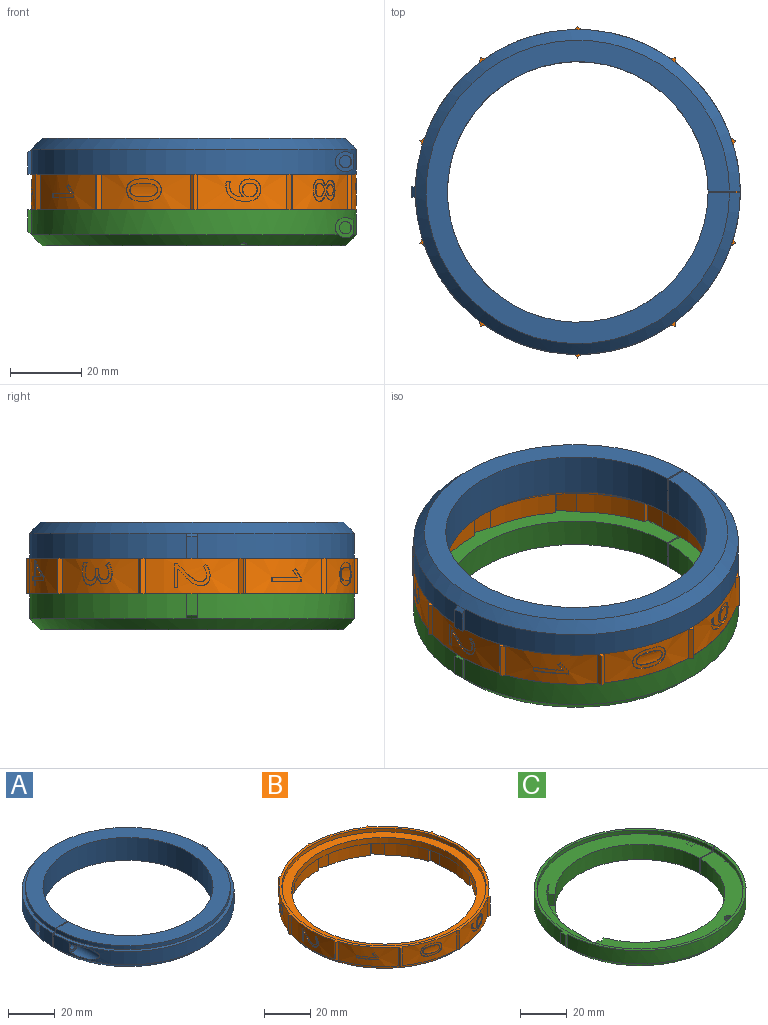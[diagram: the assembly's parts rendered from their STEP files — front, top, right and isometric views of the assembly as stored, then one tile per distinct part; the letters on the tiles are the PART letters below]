
ASSEMBLY  parts=3 mates=2
PART A: 26 faces, bbox 92x91x12 mm
  f0: plane 1.5x0.02mm, normal (0,0,-1), area 0mm2, adj f9,f23,f25
  f1: cylinder r=45.5mm len=90.97mm, axis (0,0,-1), area 970.8mm2, adj f5,f9,f11,f15,f16,f17,f18,f23
  f2: cylinder r=45.5mm len=90.97mm, axis (0,0,-1), area 920.2mm2, adj f5,f9,f10,f13,f14,f21
  f3: cylinder r=1.7mm len=8.75mm, axis (0,1,0), area 93.5mm2, adj f10,f14
  f4: cylinder r=36.5mm len=73mm, axis (0,0,-1), area 2746mm2, adj f6,f8,f10,f11
  f5: plane 92x91mm, normal (0,0,1), area 424mm2, adj f1,f2,f7,f10,f11,f21,f22,f23
  f6: plane 85x85mm, normal (0,0,-1), area 1486.1mm2, adj f4,f9,f10,f11
  f7: cylinder r=44mm len=88mm, axis (0,0,-1), area 551.9mm2, adj f5,f8,f10,f11
  f8: plane 88x88mm, normal (0,0,1), area 1893mm2, adj f4,f7,f10,f11
  f9: cone r=45.5mm half-angle=45deg, axis (0,0,1), area 1170.8mm2, adj f0,f1,f2,f6,f10,f11,f24
  f10: plane 12x9mm, normal (0,1,0), area 91.4mm2, adj f2,f3,f4,f5,f6,f7,f8,f9
  f11: plane 12x9mm, normal (0,-1,0), area 91.4mm2, adj f1,f4,f5,f6,f7,f8,f9,f12
  f12: cylinder r=1.7mm len=8.75mm, axis (0,1,0), area 93.5mm2, adj f11,f18
  f13: cylinder r=2.85mm len=13.32mm, axis (0,1,0), area 118.8mm2, adj f2,f14
  f14: plane 5.7x4.95mm, normal (0,-1,0), area 14.5mm2, adj f2,f3,f13
  f15: plane 3.75x3mm, normal (0,0,1), area 10.2mm2, adj f1,f17,f18,f19
  f16: plane 3.75x3mm, normal (0,0,-1), area 10.2mm2, adj f1,f17,f18,f20
  f17: plane 5.7x4.68mm, normal (0,-1,0), area 22mm2, adj f1,f15,f16,f19,f20
  f18: plane 5.7x5.39mm, normal (0,1,0), area 17mm2, adj f1,f12,f15,f16,f19,f20
  f19: plane 3x2.85mm, normal (-0.87,0,0.5), area 9.9mm2, adj f15,f17,f18,f20
  f20: plane 3x2.85mm, normal (-0.87,0,-0.5), area 9.9mm2, adj f16,f17,f18,f19
  f21: plane 7x1.02mm, normal (0,-1,0), area 6.7mm2, adj f2,f5,f22,f24,f25
  f22: plane 6x3mm, normal (1,0,0), area 18mm2, adj f5,f21,f23,f25
  f23: plane 7x1.02mm, normal (0,1,0), area 6.7mm2, adj f0,f1,f5,f22,f25
  f24: plane 1.5x0.02mm, normal (0,0,-1), area 0mm2, adj f9,f21,f25
  f25: plane 3x1mm, normal (0.71,0,-0.71), area 4.2mm2, adj f0,f21,f22,f23,f24
PART B: 281 faces, bbox 91x93x12 mm
  f0: cylinder r=1mm len=2mm, axis (0,0,-1), area 12.6mm2, adj f1,f39
  f1: plane 2x2mm, normal (0,0,-1), area 3.1mm2, adj f0
  f2: cylinder r=1mm len=2mm, axis (0,0,-1), area 12.6mm2, adj f3,f39
  f3: plane 2x2mm, normal (0,0,-1), area 3.1mm2, adj f2
  f4: cylinder r=1mm len=2mm, axis (0,0,-1), area 12.6mm2, adj f5,f39
  f5: plane 2x2mm, normal (0,0,-1), area 3.1mm2, adj f4
  f6: cylinder r=1mm len=2mm, axis (0,0,-1), area 12.6mm2, adj f7,f39
  f7: plane 2x2mm, normal (0,0,-1), area 3.1mm2, adj f6
  f8: cylinder r=1mm len=2mm, axis (0,0,-1), area 12.6mm2, adj f9,f39
  f9: plane 2x2mm, normal (0,0,-1), area 3.1mm2, adj f8
  f10: cylinder r=1mm len=2mm, axis (0,0,-1), area 12.6mm2, adj f11,f39
  f11: plane 2x2mm, normal (0,0,-1), area 3.1mm2, adj f10
  f12: cylinder r=1mm len=2mm, axis (0,0,-1), area 12.6mm2, adj f13,f39
  f13: plane 2x2mm, normal (0,0,-1), area 3.1mm2, adj f12
  f14: cylinder r=1mm len=2mm, axis (0,0,-1), area 12.6mm2, adj f15,f39
  f15: plane 2x2mm, normal (0,0,-1), area 3.1mm2, adj f14
  f16: cylinder r=1mm len=2mm, axis (0,0,-1), area 12.6mm2, adj f17,f39
  f17: plane 2x2mm, normal (0,0,-1), area 3.1mm2, adj f16
  f18: plane 7x1.23mm, normal (-0.95,0.31,0), area 9.1mm2, adj f19,f39,f268,f278
  f19: plane 7x5.34mm, normal (0.31,0.95,0), area 39.3mm2, adj f18,f39,f268,f270
  f20: plane 7x1.23mm, normal (-0.95,-0.31,0), area 9.1mm2, adj f21,f39,f268,f277
  f21: plane 7x5.34mm, normal (-0.31,0.95,0), area 39.3mm2, adj f20,f39,f268,f278
  f22: plane 7x1.05mm, normal (-0.59,-0.81,0), area 9.1mm2, adj f23,f39,f268,f276
  f23: plane 7x4.54mm, normal (-0.81,0.59,0), area 39.3mm2, adj f22,f39,f268,f277
  f24: plane 7x1.3mm, normal (0,-1,0), area 9.1mm2, adj f25,f39,f268,f275
  f25: plane 7x5.62mm, normal (-1,0,0), area 39.3mm2, adj f24,f39,f268,f276
  f26: plane 7x1.05mm, normal (0.59,-0.81,0), area 9.1mm2, adj f27,f39,f268,f274
  f27: plane 7x4.54mm, normal (-0.81,-0.59,0), area 39.3mm2, adj f26,f39,f268,f275
  f28: plane 7x1.23mm, normal (0.95,-0.31,0), area 9.1mm2, adj f29,f39,f268,f273
  f29: plane 7x5.34mm, normal (-0.31,-0.95,0), area 39.3mm2, adj f28,f39,f268,f274
  f30: plane 7x1.23mm, normal (0.95,0.31,0), area 9.1mm2, adj f31,f39,f268,f272
  f31: plane 7x5.34mm, normal (0.31,-0.95,0), area 39.3mm2, adj f30,f39,f268,f273
  f32: plane 7x1.05mm, normal (0.59,0.81,0), area 9.1mm2, adj f33,f39,f268,f271
  f33: plane 7x4.54mm, normal (0.81,-0.59,0), area 39.3mm2, adj f32,f39,f268,f272
  f34: plane 7x1.3mm, normal (0,1,0), area 9.1mm2, adj f35,f39,f268,f269
  f35: plane 7x5.62mm, normal (1,0,0), area 39.3mm2, adj f34,f39,f268,f271
  f36: plane 7x1.05mm, normal (-0.59,0.81,0), area 9.1mm2, adj f37,f39,f268,f270
  f37: plane 7x4.54mm, normal (0.81,0.59,0), area 39.3mm2, adj f36,f39,f268,f269
  f38: cylinder r=40mm len=80mm, axis (0,0,-1), area 754mm2, adj f54,f268
  f39: plane 88x88mm, normal (0,0,-1), area 737.2mm2, adj f0,f2,f4,f6,f8,f10,f12,f14
  f40: cylinder r=45.5mm len=26.21mm, axis (0,0,-1), area 247.6mm2, adj f50,f51,f240,f241,f242,f243,f244,f245
  f41: cylinder r=45.5mm len=21.21mm, axis (0,0,-1), area 225.9mm2, adj f50,f51,f221,f222,f223,f224,f225,f226
  f42: cylinder r=45.5mm len=24.93mm, axis (0,0,-1), area 243.7mm2, adj f50,f51,f198,f199,f200,f201,f202,f203
  f43: cylinder r=45.5mm len=24.93mm, axis (0,0,-1), area 231.8mm2, adj f50,f51,f182,f183,f184,f185,f186,f187
  f44: cylinder r=45.5mm len=21.21mm, axis (0,0,-1), area 242.3mm2, adj f50,f51,f155,f156,f157,f158,f159,f160
  f45: cylinder r=45.5mm len=26.21mm, axis (0,0,-1), area 244.2mm2, adj f50,f51,f134,f135,f136,f137,f138,f139
  f46: cylinder r=45.5mm len=21.21mm, axis (0,0,-1), area 251.4mm2, adj f50,f51,f124,f125,f126,f127,f128,f129
  f47: cylinder r=45.5mm len=24.93mm, axis (0,0,-1), area 214.8mm2, adj f50,f51,f113,f114,f115,f116,f120,f121
  f48: cylinder r=45.5mm len=21.21mm, axis (0,0,-1), area 223.1mm2, adj f50,f51,f87,f88,f89,f90,f91,f92
  f49: cylinder r=45.5mm len=24.93mm, axis (0,0,-1), area 225.9mm2, adj f50,f51,f60,f61,f62,f63,f64,f65
  f50: plane 92.98x91mm, normal (0,0,1), area 362.3mm2, adj f40,f41,f42,f43,f44,f45,f46,f47
  f51: plane 92.98x91mm, normal (0,0,-1), area 431.6mm2, adj f40,f41,f42,f43,f44,f45,f46,f47
  f52: cylinder r=44mm len=88mm, axis (0,0,1), area 552.9mm2, adj f39,f51
  f53: cylinder r=44.25mm len=88.5mm, axis (0,0,1), area 556.1mm2, adj f50,f54
  f54: plane 88.5x88.5mm, normal (0,0,1), area 1124.9mm2, adj f38,f53
  f55: extruded ~1.74x0.9mm, area 0.5mm2, adj f56,f73,f77,f78
  f56: extruded ~1.35x0.67mm, area 0.5mm2, adj f55,f57,f77,f78
  f57: extruded ~1.45x0.83mm, area 0.5mm2, adj f56,f58,f77,f78
  f58: extruded ~1.81x0.92mm, area 0.6mm2, adj f57,f59,f77,f78
  f59: extruded ~1.29x0.69mm, area 0.4mm2, adj f58,f72,f77,f78
  f60: extruded ~1.17x0.34mm, area 0.4mm2, adj f49,f61,f75,f77
  f61: extruded ~5.72x4.33mm, area 2.5mm2, adj f49,f60,f62,f77
  f62: extruded ~3.2x1.43mm, area 1mm2, adj f49,f61,f63,f77
  f63: extruded ~2.36x1.23mm, area 0.8mm2, adj f49,f62,f64,f77
  f64: extruded ~2.2x0.97mm, area 0.7mm2, adj f49,f63,f65,f77
  f65: extruded ~2.46x1.19mm, area 0.8mm2, adj f49,f64,f66,f77
  f66: extruded ~2.21x1mm, area 0.7mm2, adj f49,f65,f67,f77
  f67: extruded ~2.07x0.86mm, area 0.7mm2, adj f49,f66,f68,f77
  f68: extruded ~2.09x1.2mm, area 0.8mm2, adj f49,f67,f69,f77
  f69: plane 0.29x0.09mm, normal (0.95,0.31,0), area 0mm2, adj f49,f68,f70,f77
  f70: extruded ~3.01x1.33mm, area 1mm2, adj f49,f69,f71,f77
  f71: extruded ~2.28x1.03mm, area 0.8mm2, adj f49,f70,f76,f77
  f72: extruded ~1.45x0.62mm, area 0.5mm2, adj f59,f74,f77,f78
  f73: extruded ~1.54x0.78mm, area 0.5mm2, adj f55,f74,f77,f78
  f74: extruded ~1.33x0.6mm, area 0.4mm2, adj f72,f73,f77,f78
  f75: plane 1.13x0.51mm, normal (0,0,-1), area 0.3mm2, adj f49,f60,f76,f77
  f76: extruded ~1.13x0.35mm, area 0.3mm2, adj f49,f71,f75,f77
  f77: cylinder r=45.5mm len=9.7mm, axis (0,0,-1), area 26.6mm2, adj f55,f56,f57,f58,f59,f60,f61,f62
  f78: cylinder r=45.5mm len=4.07mm, axis (0,0,-1), area 12mm2, adj f55,f56,f57,f58,f59,f72,f73,f74
  f79: plane 0.26x0.22mm, normal (0.53,0.73,-0.43), area 0.1mm2, adj f80,f99,f105,f106
  f80: extruded ~1.45x0.94mm, area 0.4mm2, adj f79,f81,f105,f106
  f81: extruded ~1.05x0.88mm, area 0.3mm2, adj f80,f82,f105,f106
  f82: extruded ~1.2x1mm, area 0.3mm2, adj f81,f98,f105,f106
  f83: extruded ~1.26x0.85mm, area 0.4mm2, adj f84,f103,f105,f107
  f84: extruded ~1.01x0.85mm, area 0.3mm2, adj f83,f85,f105,f107
  f85: extruded ~1.03x0.87mm, area 0.3mm2, adj f84,f86,f105,f107
  f86: extruded ~1.14x0.46mm, area 0.3mm2, adj f85,f96,f105,f107
  f87: extruded ~2.16x1.78mm, area 0.8mm2, adj f48,f88,f101,f105
  f88: extruded ~1.64x1.34mm, area 0.5mm2, adj f48,f87,f89,f105
  f89: extruded ~2.02x0.71mm, area 0.5mm2, adj f48,f88,f90,f105
  f90: extruded ~2x0.71mm, area 0.5mm2, adj f48,f89,f91,f105
  f91: extruded ~1.63x1.33mm, area 0.5mm2, adj f48,f90,f92,f105
  f92: extruded ~2.22x1.74mm, area 0.8mm2, adj f48,f91,f93,f105
  f93: extruded ~2.34x1.91mm, area 0.9mm2, adj f48,f92,f94,f105
  f94: extruded ~1.82x1.48mm, area 0.6mm2, adj f48,f93,f95,f105
  f95: extruded ~2.29x0.76mm, area 0.6mm2, adj f48,f94,f97,f105
  f96: extruded ~1.17x0.46mm, area 0.3mm2, adj f86,f104,f105,f107
  f97: extruded ~2.26x0.8mm, area 0.6mm2, adj f48,f95,f102,f105
  f98: extruded ~1.43x0.53mm, area 0.4mm2, adj f82,f100,f105,f106
  f99: extruded ~1.97x1.72mm, area 0.7mm2, adj f79,f100,f105,f106
  f100: extruded ~1.87x1.53mm, area 0.7mm2, adj f98,f99,f105,f106
  f101: extruded ~2.34x2.09mm, area 0.9mm2, adj f48,f87,f102,f105
  f102: extruded ~1.83x1.48mm, area 0.6mm2, adj f48,f97,f101,f105
  f103: extruded ~1.71x1.57mm, area 0.7mm2, adj f83,f104,f105,f107
  f104: extruded ~1.03x0.87mm, area 0.3mm2, adj f96,f103,f105,f107
  f105: cylinder r=45.5mm len=8.25mm, axis (0,0,-1), area 30.7mm2, adj f79,f80,f81,f82,f83,f84,f85,f86
  f106: cylinder r=45.5mm len=3.8mm, axis (0,0,-1), area 10.9mm2, adj f79,f80,f81,f82,f98,f99,f100
  f107: cylinder r=45.5mm len=3.17mm, axis (0,0,-1), area 6.8mm2, adj f83,f84,f85,f86,f96,f103,f104
  f108: extruded ~1.44x1mm, area 0.5mm2, adj f109,f118,f122,f123
  f109: extruded ~3.07x1.3mm, area 0.8mm2, adj f108,f110,f122,f123
  f110: extruded ~3.05x1.29mm, area 0.8mm2, adj f109,f111,f122,f123
  f111: extruded ~1.44x1mm, area 0.5mm2, adj f110,f112,f122,f123
  f112: extruded ~1.46x1.01mm, area 0.5mm2, adj f111,f117,f122,f123
  f113: extruded ~5.03x3.18mm, area 1.7mm2, adj f47,f114,f120,f122
  f114: extruded ~3.73x1.56mm, area 1mm2, adj f47,f113,f115,f122
  f115: extruded ~2.38x1.37mm, area 0.7mm2, adj f47,f114,f116,f122
  f116: extruded ~5.02x3.16mm, area 1.7mm2, adj f47,f115,f121,f122
  f117: extruded ~3.05x1.29mm, area 0.8mm2, adj f112,f119,f122,f123
  f118: extruded ~1.46x1.01mm, area 0.5mm2, adj f108,f119,f122,f123
  f119: extruded ~3.06x1.3mm, area 0.8mm2, adj f117,f118,f122,f123
  f120: extruded ~2.35x1.37mm, area 0.7mm2, adj f47,f113,f121,f122
  f121: extruded ~3.74x1.56mm, area 1mm2, adj f47,f116,f120,f122
  f122: cylinder r=45.5mm len=9.71mm, axis (0,0,-1), area 27.5mm2, adj f108,f109,f110,f111,f112,f113,f114,f115
  f123: cylinder r=45.5mm len=7.7mm, axis (0,0,-1), area 23.7mm2, adj f108,f109,f110,f111,f112,f117,f118,f119
  f124: plane 1.19x0.2mm, normal (0.59,-0.81,0), area 0.3mm2, adj f46,f125,f131,f133
  f125: plane 8.17x6.02mm, normal (0,0,1), area 2.5mm2, adj f46,f124,f126,f133
  f126: plane 1.02x0.2mm, normal (-0.59,0.81,0), area 0.3mm2, adj f46,f125,f132,f133
  f127: plane 0.79x0.73mm, normal (0.36,-0.5,-0.79), area 0.3mm2, adj f46,f128,f132,f133
  f128: plane 1x0.78mm, normal (0.45,-0.63,0.63), area 0.3mm2, adj f46,f127,f129,f133
  f129: extruded ~0.82x0.8mm, area 0.3mm2, adj f46,f128,f130,f133
  f130: extruded ~2.2x1.75mm, area 0.6mm2, adj f46,f129,f131,f133
  f131: plane 5.31x3.63mm, normal (0,0,-1), area 1.5mm2, adj f46,f124,f130,f133
  f132: plane 2.6x1.69mm, normal (-0.46,0.64,-0.62), area 0.8mm2, adj f46,f126,f127,f133
  f133: cylinder r=45.5mm len=8.03mm, axis (0,0,-1), area 14.5mm2, adj f124,f125,f126,f127,f128,f129,f130,f131
  f134: plane 1.04x0.35mm, normal (0,0,1), area 0.3mm2, adj f45,f135,f152,f154
  f135: plane 5.1x0.25mm, normal (0,1,0), area 1.3mm2, adj f45,f134,f136,f154
  f136: plane 0.25x0.05mm, normal (0,0,1), area 0mm2, adj f45,f135,f137,f154
  f137: plane 2.17x2.12mm, normal (0,-0.71,0.7), area 0.8mm2, adj f45,f136,f138,f154
  f138: extruded ~2.33x1.98mm, area 0.8mm2, adj f45,f137,f139,f154
  f139: extruded ~1.87x0.53mm, area 0.5mm2, adj f45,f138,f140,f154
  f140: extruded ~1.92x0.79mm, area 0.5mm2, adj f45,f139,f141,f154
  f141: extruded ~2.19x0.72mm, area 0.6mm2, adj f45,f140,f142,f154
  f142: extruded ~2.98x1.14mm, area 0.8mm2, adj f45,f141,f143,f154
  f143: plane 0.77x0.6mm, normal (0,-0.61,-0.79), area 0.2mm2, adj f45,f142,f144,f154
  f144: extruded ~1.23x0.74mm, area 0.4mm2, adj f45,f143,f145,f154
  f145: extruded ~1.17x0.27mm, area 0.3mm2, adj f45,f144,f146,f154
  f146: extruded ~1.34x0.46mm, area 0.4mm2, adj f45,f145,f147,f154
  f147: extruded ~1.26x0.48mm, area 0.3mm2, adj f45,f146,f148,f154
  f148: extruded ~1.05x0.29mm, area 0.3mm2, adj f45,f147,f149,f154
  f149: extruded ~1x0.57mm, area 0.3mm2, adj f45,f148,f150,f154
  f150: extruded ~1.72x1.57mm, area 0.6mm2, adj f45,f149,f151,f154
  f151: plane 2.63x2.61mm, normal (0,0.71,-0.71), area 0.9mm2, adj f45,f150,f153,f154
  f152: plane 6.52x0.25mm, normal (0,-1,0), area 1.6mm2, adj f45,f134,f153,f154
  f153: plane 0.97x0.35mm, normal (0,0,-1), area 0.2mm2, adj f45,f151,f152,f154
  f154: cylinder r=45.5mm len=10.06mm, axis (0,0,-1), area 21.7mm2, adj f134,f135,f136,f137,f138,f139,f140,f141
  f155: extruded ~1.59x0.81mm, area 0.5mm2, adj f44,f156,f176,f178
  f156: extruded ~1.45x1.17mm, area 0.4mm2, adj f44,f155,f157,f178
  f157: extruded ~1.68x1.37mm, area 0.5mm2, adj f44,f156,f158,f178
  f158: extruded ~2.18x0.73mm, area 0.6mm2, adj f44,f157,f159,f178
  f159: extruded ~2.96x1.03mm, area 0.8mm2, adj f44,f158,f160,f178
  f160: plane 0.87x0.65mm, normal (-0.35,-0.48,-0.81), area 0.3mm2, adj f44,f159,f161,f178
  f161: extruded ~2.33x0.85mm, area 0.6mm2, adj f44,f160,f162,f178
  f162: extruded ~1.23x0.49mm, area 0.3mm2, adj f44,f161,f163,f178
  f163: extruded ~1.08x0.91mm, area 0.3mm2, adj f44,f162,f164,f178
  f164: extruded ~1.28x1.05mm, area 0.4mm2, adj f44,f163,f165,f178
  f165: extruded ~1.68x0.57mm, area 0.4mm2, adj f44,f164,f166,f178
  f166: plane 0.9x0.2mm, normal (0.59,0.81,0), area 0.2mm2, adj f44,f165,f167,f178
  f167: plane 0.98x0.8mm, normal (0,0,-1), area 0.3mm2, adj f44,f166,f168,f178
  f168: plane 0.9x0.2mm, normal (-0.59,-0.81,0), area 0.2mm2, adj f44,f167,f169,f178
  f169: extruded ~2.58x1.59mm, area 0.9mm2, adj f44,f168,f170,f178
  f170: extruded ~2.4x1.81mm, area 0.9mm2, adj f44,f169,f171,f178
  f171: extruded ~2.6x0.71mm, area 0.7mm2, adj f44,f170,f172,f178
  f172: plane 1.02x0.96mm, normal (0,0,-1), area 0.3mm2, adj f44,f171,f173,f178
  f173: extruded ~2.63x0.61mm, area 0.7mm2, adj f44,f172,f174,f178
  f174: extruded ~2.71x0.84mm, area 0.7mm2, adj f44,f173,f175,f178
  f175: extruded ~1.99x1.6mm, area 0.6mm2, adj f44,f174,f177,f178
  f176: plane 0.23x0.18mm, normal (0,0,1), area 0mm2, adj f44,f155,f177,f178
  f177: extruded ~2.45x2.09mm, area 0.9mm2, adj f44,f175,f176,f178
  f178: cylinder r=45.5mm len=8.24mm, axis (0,0,-1), area 23.6mm2, adj f155,f156,f157,f158,f159,f160,f161,f162
  f179: plane 3.37x0.24mm, normal (0.95,0.31,0), area 0.8mm2, adj f180,f192,f196,f197
  f180: plane 3.99x2.79mm, normal (-0.53,-0.17,0.83), area 1.2mm2, adj f179,f181,f196,f197
  f181: extruded ~1.26x0.69mm, area 0.3mm2, adj f180,f191,f196,f197
  f182: plane 1.17x0.53mm, normal (0,0,1), area 0.3mm2, adj f43,f183,f194,f196
  f183: plane 1.45x0.24mm, normal (0.95,0.31,0), area 0.4mm2, adj f43,f182,f184,f196
  f184: plane 6.3x2.51mm, normal (0,0,1), area 1.7mm2, adj f43,f183,f185,f196
  f185: plane 1.27x0.24mm, normal (0.95,0.31,0), area 0.3mm2, adj f43,f184,f186,f196
  f186: plane 6.35x4.51mm, normal (0.53,0.17,-0.83), area 2mm2, adj f43,f185,f187,f196
  f187: plane 1.12x0.52mm, normal (0,0,-1), area 0.3mm2, adj f43,f186,f188,f196
  f188: plane 4.58x0.24mm, normal (-0.95,-0.31,0), area 1.1mm2, adj f43,f187,f189,f196
  f189: plane 2.25x0.74mm, normal (0,0,-1), area 0.6mm2, adj f43,f188,f190,f196
  f190: plane 1.19x0.24mm, normal (-0.95,-0.31,0), area 0.3mm2, adj f43,f189,f195,f196
  f191: plane 0.24x0.08mm, normal (-0.95,-0.31,0), area 0mm2, adj f181,f193,f196,f197
  f192: plane 2.38x0.96mm, normal (0,0,-1), area 0.6mm2, adj f179,f193,f196,f197
  f193: extruded ~2.91x1.28mm, area 0.7mm2, adj f191,f192,f196,f197
  f194: plane 1.45x0.24mm, normal (-0.95,-0.31,0), area 0.4mm2, adj f43,f182,f195,f196
  f195: plane 2.25x0.74mm, normal (0,0,1), area 0.6mm2, adj f43,f190,f194,f196
  f196: cylinder r=45.5mm len=9.48mm, axis (0,0,-1), area 25.5mm2, adj f179,f180,f181,f182,f183,f184,f185,f186
  f197: cylinder r=45.5mm len=5.04mm, axis (0,0,-1), area 8.6mm2, adj f179,f180,f181,f191,f192,f193
  f198: extruded ~2.41x0.61mm, area 0.6mm2, adj f42,f199,f213,f215
  f199: extruded ~2.64x0.93mm, area 0.7mm2, adj f42,f198,f200,f215
  f200: extruded ~2.46x1.15mm, area 0.7mm2, adj f42,f199,f201,f215
  f201: extruded ~2.11x0.93mm, area 0.6mm2, adj f42,f200,f202,f215
  f202: extruded ~2.3x0.82mm, area 0.6mm2, adj f42,f201,f203,f215
  f203: extruded ~1.42x0.28mm, area 0.4mm2, adj f42,f202,f204,f215
  f204: plane 2.82x0.97mm, normal (-0.09,0.03,1), area 0.7mm2, adj f42,f203,f205,f215
  f205: plane 3.61x0.24mm, normal (-0.95,0.31,0), area 0.9mm2, adj f42,f204,f206,f215
  f206: plane 1.18x0.48mm, normal (0,0,1), area 0.3mm2, adj f42,f205,f207,f215
  f207: plane 4.68x0.24mm, normal (0.95,-0.31,0), area 1.2mm2, adj f42,f206,f208,f215
  f208: plane 4.6x1.43mm, normal (0.08,-0.02,-1), area 1.2mm2, adj f42,f207,f209,f215
  f209: plane 0.61x0.44mm, normal (-0.8,0.26,-0.53), area 0.2mm2, adj f42,f208,f210,f215
  f210: extruded ~1.57x0.29mm, area 0.4mm2, adj f42,f209,f211,f215
  f211: extruded ~2.33x1.99mm, area 0.9mm2, adj f42,f210,f212,f215
  f212: extruded ~2.28x2.15mm, area 0.9mm2, adj f42,f211,f214,f215
  f213: plane 1.16x0.7mm, normal (0,0,-1), area 0.3mm2, adj f42,f198,f214,f215
  f214: extruded ~2.44x0.71mm, area 0.6mm2, adj f42,f212,f213,f215
  f215: cylinder r=45.5mm len=9.55mm, axis (0,0,-1), area 22.2mm2, adj f198,f199,f200,f201,f202,f203,f204,f205
  f216: extruded ~1.58x1.28mm, area 0.4mm2, adj f217,f234,f238,f239
  f217: extruded ~1.35x0.66mm, area 0.4mm2, adj f216,f218,f238,f239
  f218: extruded ~1.44x0.79mm, area 0.4mm2, adj f217,f219,f238,f239
  f219: extruded ~1.64x1.33mm, area 0.5mm2, adj f218,f220,f238,f239
  f220: extruded ~1.18x0.96mm, area 0.4mm2, adj f219,f233,f238,f239
  f221: extruded ~1.17x0.29mm, area 0.3mm2, adj f41,f222,f236,f238
  f222: extruded ~5.02x4.33mm, area 2.1mm2, adj f41,f221,f223,f238
  f223: extruded ~2.86x2.24mm, area 0.9mm2, adj f41,f222,f224,f238
  f224: extruded ~2.36x1.14mm, area 0.7mm2, adj f41,f223,f225,f238
  f225: extruded ~2.19x0.92mm, area 0.6mm2, adj f41,f224,f226,f238
  f226: extruded ~2.22x1.77mm, area 0.7mm2, adj f41,f225,f227,f238
  f227: extruded ~1.95x1.53mm, area 0.6mm2, adj f41,f226,f228,f238
  f228: extruded ~2.07x0.81mm, area 0.6mm2, adj f41,f227,f229,f238
  f229: extruded ~2.08x1.09mm, area 0.6mm2, adj f41,f228,f230,f238
  f230: plane 0.2x0.15mm, normal (0.59,-0.81,0), area 0mm2, adj f41,f229,f231,f238
  f231: extruded ~2.66x2.07mm, area 0.8mm2, adj f41,f230,f232,f238
  f232: extruded ~2.28x0.97mm, area 0.6mm2, adj f41,f231,f237,f238
  f233: extruded ~1.44x0.59mm, area 0.4mm2, adj f220,f235,f238,f239
  f234: extruded ~1.39x1.12mm, area 0.4mm2, adj f216,f235,f238,f239
  f235: extruded ~1.33x0.58mm, area 0.4mm2, adj f233,f234,f238,f239
  f236: plane 0.94x0.9mm, normal (0,0,1), area 0.3mm2, adj f41,f221,f237,f238
  f237: extruded ~1.13x0.31mm, area 0.3mm2, adj f41,f232,f236,f238
  f238: cylinder r=45.5mm len=8.25mm, axis (0,0,-1), area 26.7mm2, adj f216,f217,f218,f219,f220,f221,f222,f223
  f239: cylinder r=45.5mm len=3.82mm, axis (0,0,-1), area 12mm2, adj f216,f217,f218,f219,f220,f233,f234,f235
  f240: plane 1.32x0.25mm, normal (0,1,0), area 0.3mm2, adj f40,f241,f245,f247
  f241: plane 8.94x3.77mm, normal (0,0.39,0.92), area 2.4mm2, adj f40,f240,f246,f247
  f242: plane 6.37x0.25mm, normal (0,-1,0), area 1.6mm2, adj f40,f243,f246,f247
  f243: plane 1.13x0.36mm, normal (0,0,-1), area 0.3mm2, adj f40,f242,f244,f247
  f244: plane 5.11x0.25mm, normal (0,1,0), area 1.3mm2, adj f40,f243,f245,f247
  f245: plane 8.79x3.82mm, normal (0,-0.4,-0.92), area 2.4mm2, adj f40,f240,f244,f247
  f246: plane 0.98x0.35mm, normal (0,0,1), area 0.2mm2, adj f40,f241,f242,f247
  f247: cylinder r=45.5mm len=9.92mm, axis (0,0,-1), area 18.3mm2, adj f240,f241,f242,f243,f244,f245,f246
  f248: plane 10x1mm, normal (-0.71,0.71,0), area 14.1mm2, adj f43,f50,f51,f249
  f249: plane 10x1mm, normal (0.71,0.71,0), area 14.1mm2, adj f42,f50,f51,f248
  f250: plane 10x1.4mm, normal (-0.99,0.16,0), area 14.1mm2, adj f44,f50,f51,f251
  f251: plane 10x1.4mm, normal (0.16,0.99,0), area 14.1mm2, adj f43,f50,f51,f250
  f252: plane 10x1.26mm, normal (-0.89,-0.45,0), area 14.1mm2, adj f45,f50,f51,f253
  f253: plane 10x1.26mm, normal (-0.45,0.89,0), area 14.1mm2, adj f44,f50,f51,f252
  f254: plane 10x1.26mm, normal (-0.45,-0.89,0), area 14.1mm2, adj f46,f50,f51,f255
  f255: plane 10x1.26mm, normal (-0.89,0.45,0), area 14.1mm2, adj f45,f50,f51,f254
  f256: plane 10x1.4mm, normal (0.16,-0.99,0), area 14.1mm2, adj f47,f50,f51,f257
  f257: plane 10x1.4mm, normal (-0.99,-0.16,0), area 14.1mm2, adj f46,f50,f51,f256
  f258: plane 10x1mm, normal (0.71,-0.71,0), area 14.1mm2, adj f49,f50,f51,f259
  f259: plane 10x1mm, normal (-0.71,-0.71,0), area 14.1mm2, adj f47,f50,f51,f258
  f260: plane 10x1.4mm, normal (0.99,-0.16,0), area 14.1mm2, adj f48,f50,f51,f261
  f261: plane 10x1.4mm, normal (-0.16,-0.99,0), area 14.1mm2, adj f49,f50,f51,f260
  f262: plane 10x1.26mm, normal (0.89,0.45,0), area 14.1mm2, adj f40,f50,f51,f263
  f263: plane 10x1.26mm, normal (0.45,-0.89,0), area 14.1mm2, adj f48,f50,f51,f262
  f264: plane 10x1.26mm, normal (0.45,0.89,0), area 14.1mm2, adj f41,f50,f51,f265
  f265: plane 10x1.26mm, normal (0.89,-0.45,0), area 14.1mm2, adj f40,f50,f51,f264
  f266: plane 10x1.4mm, normal (-0.16,0.99,0), area 14.1mm2, adj f42,f50,f51,f267
  f267: plane 10x1.4mm, normal (0.99,0.16,0), area 14.1mm2, adj f41,f50,f51,f266
  f268: plane 84.45x82mm, normal (0,0,-1), area 286.9mm2, adj f18,f19,f20,f21,f22,f23,f24,f25
  f269: cylinder r=41mm len=16.97mm, axis (0,0,-1), area 139.9mm2, adj f34,f37,f39,f268
  f270: cylinder r=41mm len=18.22mm, axis (0,0,-1), area 139.9mm2, adj f19,f36,f39,f268
  f271: cylinder r=41mm len=19.72mm, axis (0,0,-1), area 139.9mm2, adj f32,f35,f39,f268
  f272: cylinder r=41mm len=14.94mm, axis (0,0,-1), area 139.9mm2, adj f30,f33,f39,f268
  f273: cylinder r=41mm len=19.29mm, axis (0,0,-1), area 139.9mm2, adj f28,f31,f39,f268
  f274: cylinder r=41mm len=18.22mm, axis (0,0,-1), area 139.9mm2, adj f26,f29,f39,f268
  f275: cylinder r=41mm len=16.97mm, axis (0,0,-1), area 139.9mm2, adj f24,f27,f39,f268
  f276: cylinder r=41mm len=19.72mm, axis (0,0,-1), area 139.9mm2, adj f22,f25,f39,f268
  f277: cylinder r=41mm len=14.94mm, axis (0,0,-1), area 139.9mm2, adj f20,f23,f39,f268
  f278: cylinder r=41mm len=19.29mm, axis (0,0,-1), area 139.9mm2, adj f18,f21,f39,f268
  f279: cylinder r=1mm len=2mm, axis (0,0,-1), area 12.6mm2, adj f39,f280
  f280: plane 2x2mm, normal (0,0,-1), area 3.1mm2, adj f279
PART C: 42 faces, bbox 92x91x10 mm
  f0: cylinder r=45.5mm len=90.97mm, axis (0,0,-1), area 974.7mm2, adj f1,f8,f26,f27,f32,f35,f40
  f1: cone r=45.5mm half-angle=45deg, axis (0,0,1), area 1155.1mm2, adj f0,f2,f3,f9,f22,f26,f27,f31
  f2: plane 1.5x0.02mm, normal (0,0,-1), area 0mm2, adj f1,f37,f39
  f3: cylinder r=45.5mm len=90.97mm, axis (0,0,-1), area 926.5mm2, adj f1,f8,f22,f23,f33,f37
  f4: plane 45.99x17.02mm, normal (0,0,1), area 159.5mm2, adj f5,f7,f12,f13,f14,f19,f20,f21
  f5: cylinder r=39.5mm len=6mm, axis (0,0,1), area 9.2mm2, adj f4,f6,f13,f34
  f6: plane 88.5x88.5mm, normal (0,0,1), area 1791.4mm2, adj f5,f7,f10,f12,f13,f14,f15,f19
  f7: cylinder r=36.5mm len=73mm, axis (0,0,-1), area 1586.4mm2, adj f4,f6,f9,f21,f32,f33,f34
  f8: plane 92x91mm, normal (0,0,1), area 354.8mm2, adj f0,f3,f10,f32,f33,f35,f36,f37
  f9: plane 85x85mm, normal (0,0,-1), area 1484.1mm2, adj f1,f7,f32,f33,f41
  f10: cylinder r=44.25mm len=88.5mm, axis (0,0,1), area 555.1mm2, adj f6,f8,f32,f33
  f11: cylinder r=1.7mm len=8.75mm, axis (0,-1,0), area 93.5mm2, adj f23,f33
  f12: plane 12x6mm, normal (1,0,0), area 72mm2, adj f4,f6,f13,f14
  f13: plane 6x2.37mm, normal (0,1,0), area 14.2mm2, adj f4,f5,f6,f12
  f14: cylinder r=40mm len=32.54mm, axis (0,0,1), area 228mm2, adj f4,f6,f12,f19
  f15: cylinder r=1.9mm len=3.8mm, axis (0,0,1), area 11.9mm2, adj f6,f16
  f16: plane 3.8x3.8mm, normal (0,0,1), area 3.8mm2, adj f15,f18
  f17: plane 3.1x3.1mm, normal (0,0,1), area 4.4mm2, adj f18,f41
  f18: cylinder r=1.55mm len=3.2mm, axis (0,0,1), area 31.2mm2, adj f16,f17
  f19: plane 6x0.41mm, normal (-0.81,-0.58,0), area 3mm2, adj f4,f6,f14,f20
  f20: cylinder r=39.5mm len=6mm, axis (0,0,1), area 43.1mm2, adj f4,f6,f19,f21
  f21: plane 6x2.16mm, normal (-0.69,-0.72,0), area 18mm2, adj f4,f6,f7,f20
  f22: cylinder r=2.85mm len=13.32mm, axis (0,1,0), area 110.8mm2, adj f1,f3,f23
  f23: plane 5.7x4.95mm, normal (0,-1,0), area 14.5mm2, adj f3,f11,f22
  f24: cylinder r=1.7mm len=8.75mm, axis (0,-1,0), area 93.5mm2, adj f27,f32
  f25: plane 3x0.42mm, normal (-0.87,0,-0.5), area 1.5mm2, adj f26,f27,f28,f40
  f26: plane 5.7x5.18mm, normal (0,-1,0), area 24.4mm2, adj f0,f1,f25,f28,f29,f30,f31
  f27: plane 5.89x5.7mm, normal (0,1,0), area 19.1mm2, adj f0,f1,f24,f25,f28,f29,f30,f31
  f28: plane 3.29x3mm, normal (0,0,-1), area 9.9mm2, adj f25,f26,f27,f29
  f29: plane 3x2.85mm, normal (0.87,0,-0.5), area 9.9mm2, adj f26,f27,f28,f30
  f30: plane 3x2.85mm, normal (0.87,0,0.5), area 9.9mm2, adj f26,f27,f29,f31
  f31: plane 3.38x3mm, normal (0,0,1), area 9.1mm2, adj f1,f26,f27,f30
  f32: plane 10x9mm, normal (0,-1,0), area 60.9mm2, adj f0,f1,f6,f7,f8,f9,f10,f24
  f33: plane 10x9mm, normal (0,1,0), area 60.9mm2, adj f1,f3,f6,f7,f8,f9,f10,f11
  f34: plane 6x2.82mm, normal (-0.34,0.94,0), area 18mm2, adj f4,f5,f6,f7
  f35: plane 7x1.02mm, normal (0,1,0), area 6.7mm2, adj f0,f8,f36,f38,f39
  f36: plane 6x3mm, normal (-1,0,0), area 18mm2, adj f8,f35,f37,f39
  f37: plane 7x1.02mm, normal (0,-1,0), area 6.7mm2, adj f2,f3,f8,f36,f39
  f38: plane 1.5x0.02mm, normal (0,0,-1), area 0mm2, adj f1,f35,f39
  f39: plane 3x1mm, normal (-0.71,0,-0.71), area 4.2mm2, adj f2,f35,f36,f37,f38
  f40: plane 3x0.71mm, normal (0,0,-1), area 1.1mm2, adj f0,f25,f27
  f41: cylinder r=1mm len=3.8mm, axis (0,0,1), area 22.6mm2, adj f1,f9,f17
PLACE A rot(axis=(0,1,0),180deg) t=(-9.1,-6.33,9.39)mm
PLACE B t=(-9.1,-6.33,-5.61)mm fixed
PLACE C t=(-9.1,-6.33,-10.61)mm
MATE fastened C.f10 <-> B.f52  axis (0,0,1) through (-9.1,-6.33,-6.61)mm
MATE fastened A.f1 <-> C.f0  axis (0,0,1) through (-9.1,-6.33,7.89)mm
